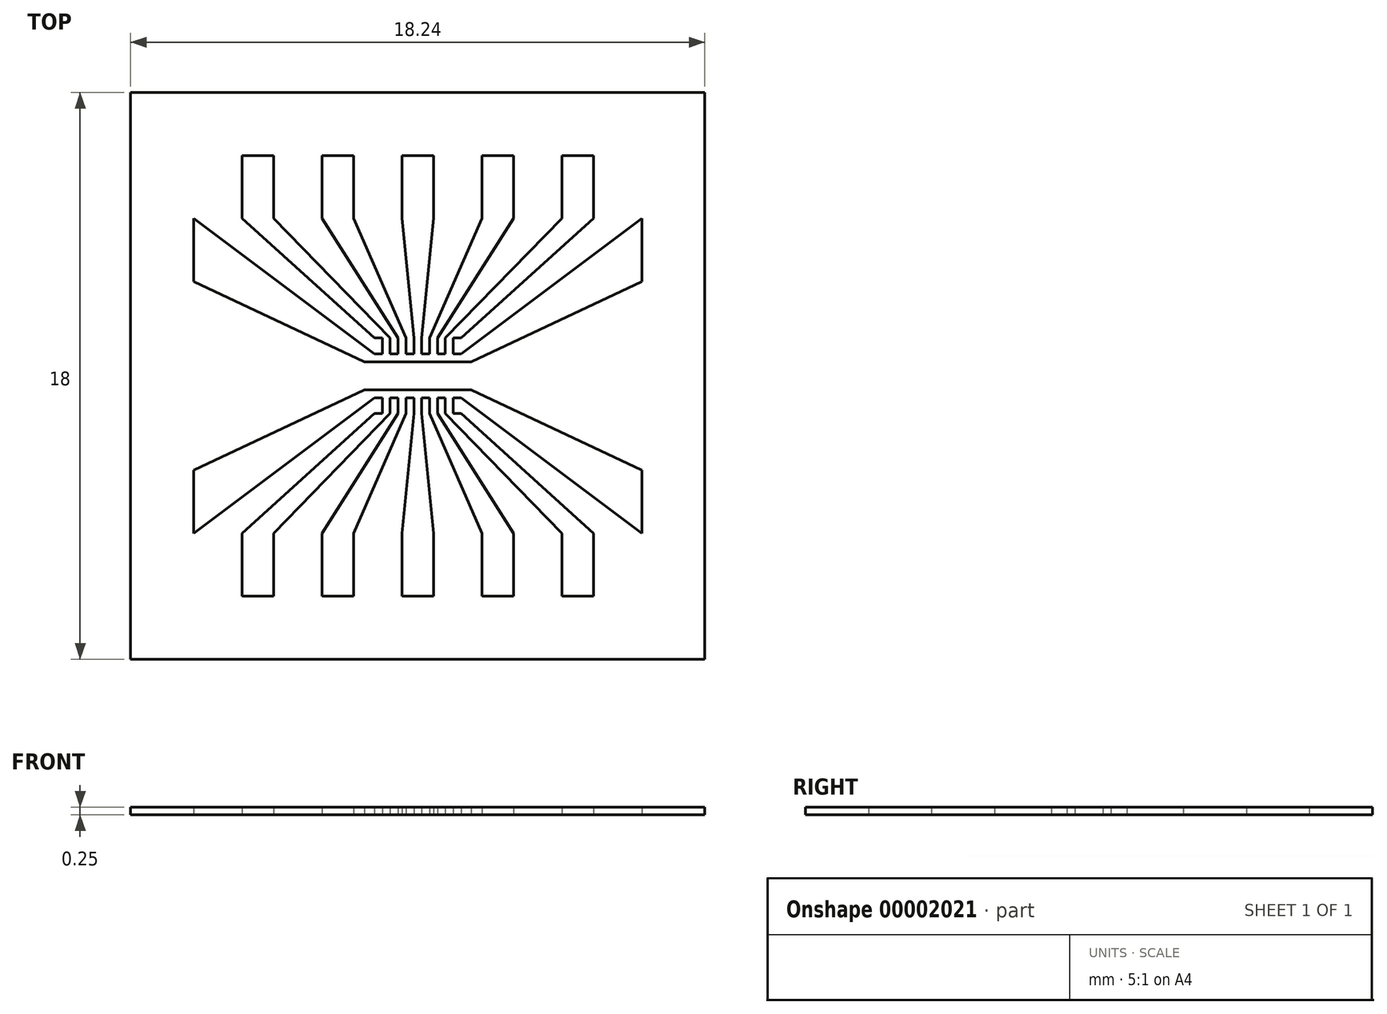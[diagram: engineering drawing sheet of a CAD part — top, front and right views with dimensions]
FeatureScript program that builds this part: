
annotation { "Feature Type Name" : "Feature", "Feature Type Description" : "" }
export const myFeature = defineFeature(function(context is Context, id is Id, definition is map)
    precondition{}
    {
        {
            var Q0;
            Q0=qCreatedBy(makeId("Top.planeOp"),FACE);
            var sketch = newSketch(context, id + "F0", { "sketchPlane" : qUnion([Q0])});
            skLineSegment(sketch, "E0.rect.bottom", {"start": v(1.7, 0.45) * mm, "end": v(-1.7, 0.45) * mm});
            skLineSegment(sketch, "E0.rect.top", {"start": v(1.7, -0.45) * mm, "end": v(-1.7, -0.45) * mm});
            skLineSegment(sketch, "E0.rect.left", {"start": v(1.7, 0.45) * mm, "end": v(1.7, -0.45) * mm, "construction": true});
            skLineSegment(sketch, "E0.rect.right", {"start": v(-1.7, 0.45) * mm, "end": v(-1.7, -0.45) * mm, "construction": true});
            skPoint(sketch, "E0.rect.middle", {"position": v(0, 0) * mm});
            skLineSegment(sketch, "E1", {"start": v(0, 0.45) * mm, "end": v(0, -0.45) * mm, "construction": true});
            skLineSegment(sketch, "E2", {"start": v(-1.7, 0) * mm, "end": v(1.7, 0) * mm, "construction": true});
            skLineSegment(sketch, "E3.bottom", {"start": v(-1.38, -0.7) * mm, "end": v(-1.13, -0.7) * mm});
            skLineSegment(sketch, "E3.top", {"start": v(-1.38, -1.2) * mm, "end": v(-1.13, -1.2) * mm});
            skLineSegment(sketch, "E3.left", {"start": v(-1.38, -0.7) * mm, "end": v(-1.38, -1.2) * mm, "construction": true});
            skLineSegment(sketch, "E3.right", {"start": v(-1.12, -0.7) * mm, "end": v(-1.12, -1.2) * mm});
            skLineSegment(sketch, "E4.bottom", {"start": v(-0.88, -0.7) * mm, "end": v(-0.63, -0.7) * mm});
            skLineSegment(sketch, "E4.top", {"start": v(-0.88, -1.2) * mm, "end": v(-0.63, -1.2) * mm, "construction": true});
            skLineSegment(sketch, "E4.left", {"start": v(-0.88, -0.7) * mm, "end": v(-0.88, -1.2) * mm});
            skLineSegment(sketch, "E4.right", {"start": v(-0.63, -0.7) * mm, "end": v(-0.63, -1.2) * mm});
            skLineSegment(sketch, "E5.bottom", {"start": v(-0.38, -0.7) * mm, "end": v(-0.12, -0.7) * mm});
            skLineSegment(sketch, "E5.top", {"start": v(-0.38, -1.2) * mm, "end": v(-0.13, -1.2) * mm, "construction": true});
            skLineSegment(sketch, "E5.left", {"start": v(-0.38, -0.7) * mm, "end": v(-0.38, -1.2) * mm});
            skLineSegment(sketch, "E5.right", {"start": v(-0.12, -0.7) * mm, "end": v(-0.12, -1.2) * mm});
            skLineSegment(sketch, "E6.bottom", {"start": v(0.12, -0.7) * mm, "end": v(0.38, -0.7) * mm});
            skLineSegment(sketch, "E6.top", {"start": v(0.13, -1.2) * mm, "end": v(0.38, -1.2) * mm, "construction": true});
            skLineSegment(sketch, "E6.left", {"start": v(0.12, -0.7) * mm, "end": v(0.12, -1.2) * mm});
            skLineSegment(sketch, "E6.right", {"start": v(0.38, -0.7) * mm, "end": v(0.38, -1.2) * mm});
            skLineSegment(sketch, "E7.bottom", {"start": v(0.63, -0.7) * mm, "end": v(0.88, -0.7) * mm});
            skLineSegment(sketch, "E7.top", {"start": v(0.63, -1.2) * mm, "end": v(0.88, -1.2) * mm, "construction": true});
            skLineSegment(sketch, "E7.left", {"start": v(0.63, -0.7) * mm, "end": v(0.63, -1.2) * mm});
            skLineSegment(sketch, "E7.right", {"start": v(0.88, -0.7) * mm, "end": v(0.88, -1.2) * mm});
            skLineSegment(sketch, "E8.bottom", {"start": v(1.13, -0.7) * mm, "end": v(1.38, -0.7) * mm});
            skLineSegment(sketch, "E8.top", {"start": v(1.13, -1.2) * mm, "end": v(1.38, -1.2) * mm});
            skLineSegment(sketch, "E8.left", {"start": v(1.12, -0.7) * mm, "end": v(1.12, -1.2) * mm});
            skLineSegment(sketch, "E8.right", {"start": v(1.38, -0.7) * mm, "end": v(1.38, -1.2) * mm, "construction": true});
            skLineSegment(sketch, "E9", {"start": v(-0.12, -0.7) * mm, "end": v(0.12, -0.7) * mm, "construction": true});
            skLineSegment(sketch, "E10", {"start": v(-0.63, -0.7) * mm, "end": v(-0.38, -0.7) * mm, "construction": true});
            skLineSegment(sketch, "E11", {"start": v(-1.13, -0.7) * mm, "end": v(-0.88, -0.7) * mm, "construction": true});
            skLineSegment(sketch, "E12", {"start": v(0.38, -0.7) * mm, "end": v(0.63, -0.7) * mm, "construction": true});
            skLineSegment(sketch, "E13", {"start": v(0.88, -0.7) * mm, "end": v(1.13, -0.7) * mm, "construction": true});
            skPoint(sketch, "E14", {"position": v(0, -0.7) * mm});
            skPoint(sketch, "E15", {"position": v(-1.25, -0.7) * mm});
            skPoint(sketch, "E16", {"position": v(-0.75, -0.7) * mm});
            skLineSegment(sketch, "E17.0.MirrorCS", {"start": v(0.12, 0.7) * mm, "end": v(0.12, 1.2) * mm});
            skLineSegment(sketch, "E17.1.MirrorCS", {"start": v(1.12, 0.7) * mm, "end": v(1.12, 1.2) * mm});
            skLineSegment(sketch, "E17.2.MirrorCS", {"start": v(0.63, 1.2) * mm, "end": v(0.88, 1.2) * mm, "construction": true});
            skLineSegment(sketch, "E17.3.MirrorCS", {"start": v(0.13, 0.7) * mm, "end": v(0.38, 0.7) * mm});
            skLineSegment(sketch, "E17.4.MirrorCS", {"start": v(0.88, 0.7) * mm, "end": v(1.13, 0.7) * mm, "construction": true});
            skLineSegment(sketch, "E17.5.MirrorCS", {"start": v(0.63, 0.7) * mm, "end": v(0.88, 0.7) * mm});
            skLineSegment(sketch, "E17.6.MirrorCS", {"start": v(-0.13, 0.7) * mm, "end": v(0.13, 0.7) * mm, "construction": true});
            skLineSegment(sketch, "E17.7.MirrorCS", {"start": v(-0.63, 0.7) * mm, "end": v(-0.38, 0.7) * mm, "construction": true});
            skLineSegment(sketch, "E17.8.MirrorCS", {"start": v(-0.63, 0.7) * mm, "end": v(-0.63, 1.2) * mm});
            skLineSegment(sketch, "E17.9.MirrorCS", {"start": v(0.88, 0.7) * mm, "end": v(0.88, 1.2) * mm});
            skLineSegment(sketch, "E17.10.MirrorCS", {"start": v(-0.38, 1.2) * mm, "end": v(-0.13, 1.2) * mm, "construction": true});
            skLineSegment(sketch, "E17.11.MirrorCS", {"start": v(1.13, 1.2) * mm, "end": v(1.38, 1.2) * mm});
            skLineSegment(sketch, "E17.12.MirrorCS", {"start": v(0.13, 1.2) * mm, "end": v(0.38, 1.2) * mm, "construction": true});
            skLineSegment(sketch, "E17.13.MirrorCS", {"start": v(-0.38, 0.7) * mm, "end": v(-0.38, 1.2) * mm});
            skLineSegment(sketch, "E17.14.MirrorCS", {"start": v(-0.38, 0.7) * mm, "end": v(-0.13, 0.7) * mm});
            skLineSegment(sketch, "E17.15.MirrorCS", {"start": v(1.13, 0.7) * mm, "end": v(1.38, 0.7) * mm});
            skLineSegment(sketch, "E17.16.MirrorCS", {"start": v(0.38, 0.7) * mm, "end": v(0.63, 0.7) * mm, "construction": true});
            skLineSegment(sketch, "E17.17.MirrorCS", {"start": v(-1.13, 0.7) * mm, "end": v(-0.88, 0.7) * mm, "construction": true});
            skLineSegment(sketch, "E17.18.MirrorCS", {"start": v(-1.38, 0.7) * mm, "end": v(-1.38, 1.2) * mm, "construction": true});
            skLineSegment(sketch, "E17.19.MirrorCS", {"start": v(-1.38, 1.2) * mm, "end": v(-1.13, 1.2) * mm});
            skLineSegment(sketch, "E17.20.MirrorCS", {"start": v(-0.88, 0.7) * mm, "end": v(-0.63, 0.7) * mm});
            skLineSegment(sketch, "E17.21.MirrorCS", {"start": v(-1.12, 0.7) * mm, "end": v(-1.12, 1.2) * mm});
            skLineSegment(sketch, "E17.22.MirrorCS", {"start": v(-1.38, 0.7) * mm, "end": v(-1.13, 0.7) * mm});
            skLineSegment(sketch, "E17.23.MirrorCS", {"start": v(-0.88, 0.7) * mm, "end": v(-0.88, 1.2) * mm});
            skLineSegment(sketch, "E17.24.MirrorCS", {"start": v(0.62, 0.7) * mm, "end": v(0.62, 1.2) * mm});
            skLineSegment(sketch, "E17.25.MirrorCS", {"start": v(1.38, 0.7) * mm, "end": v(1.38, 1.2) * mm, "construction": true});
            skLineSegment(sketch, "E17.26.MirrorCS", {"start": v(0.38, 0.7) * mm, "end": v(0.38, 1.2) * mm});
            skLineSegment(sketch, "E17.27.MirrorCS", {"start": v(-0.12, 0.7) * mm, "end": v(-0.13, 1.2) * mm});
            skLineSegment(sketch, "E17.28.MirrorCS", {"start": v(-0.88, 1.2) * mm, "end": v(-0.63, 1.2) * mm, "construction": true});
            skLineSegment(sketch, "E18.rect.bottom", {"start": v(-0.5, -5) * mm, "end": v(-2.04, -5) * mm, "construction": true});
            skLineSegment(sketch, "E18.rect.top", {"start": v(-0.5, -7) * mm, "end": v(-2.04, -7) * mm});
            skLineSegment(sketch, "E18.rect.left", {"start": v(-0.5, -5) * mm, "end": v(-0.5, -7) * mm});
            skLineSegment(sketch, "E18.rect.right", {"start": v(-2.04, -5) * mm, "end": v(-2.04, -7) * mm});
            skPoint(sketch, "E18.rect.middle", {"position": v(-1.27, -6) * mm});
            skLineSegment(sketch, "E19.rect.bottom", {"start": v(2.04, -5) * mm, "end": v(0.5, -5) * mm, "construction": true});
            skLineSegment(sketch, "E19.rect.top", {"start": v(2.04, -7) * mm, "end": v(0.5, -7) * mm});
            skLineSegment(sketch, "E19.rect.left", {"start": v(2.04, -5) * mm, "end": v(2.04, -7) * mm});
            skLineSegment(sketch, "E19.rect.right", {"start": v(0.5, -5) * mm, "end": v(0.5, -7) * mm});
            skPoint(sketch, "E19.rect.middle", {"position": v(1.27, -6) * mm});
            skLineSegment(sketch, "E20.rect.bottom", {"start": v(4.58, -5) * mm, "end": v(3.04, -5) * mm, "construction": true});
            skLineSegment(sketch, "E20.rect.top", {"start": v(4.58, -7) * mm, "end": v(3.04, -7) * mm});
            skLineSegment(sketch, "E20.rect.left", {"start": v(4.58, -5) * mm, "end": v(4.58, -7) * mm});
            skLineSegment(sketch, "E20.rect.right", {"start": v(3.04, -5) * mm, "end": v(3.04, -7) * mm});
            skPoint(sketch, "E20.rect.middle", {"position": v(3.8, -6) * mm});
            skLineSegment(sketch, "E21.rect.bottom", {"start": v(7.12, -5) * mm, "end": v(5.58, -5) * mm, "construction": true});
            skLineSegment(sketch, "E21.rect.top", {"start": v(7.12, -7) * mm, "end": v(5.58, -7) * mm});
            skLineSegment(sketch, "E21.rect.left", {"start": v(7.12, -5) * mm, "end": v(7.12, -7) * mm});
            skLineSegment(sketch, "E21.rect.right", {"start": v(5.58, -5) * mm, "end": v(5.58, -7) * mm});
            skPoint(sketch, "E21.rect.middle", {"position": v(6.35, -6) * mm});
            skLineSegment(sketch, "E22.rect.bottom", {"start": v(-3.04, -5) * mm, "end": v(-4.58, -5) * mm, "construction": true});
            skLineSegment(sketch, "E22.rect.top", {"start": v(-3.04, -7) * mm, "end": v(-4.58, -7) * mm});
            skLineSegment(sketch, "E22.rect.left", {"start": v(-3.04, -5) * mm, "end": v(-3.04, -7) * mm});
            skLineSegment(sketch, "E22.rect.right", {"start": v(-4.58, -5) * mm, "end": v(-4.58, -7) * mm});
            skPoint(sketch, "E22.rect.middle", {"position": v(-3.8, -6) * mm});
            skLineSegment(sketch, "E23.rect.bottom", {"start": v(-5.58, -5) * mm, "end": v(-7.12, -5) * mm, "construction": true});
            skLineSegment(sketch, "E23.rect.top", {"start": v(-5.58, -7) * mm, "end": v(-7.12, -7) * mm});
            skLineSegment(sketch, "E23.rect.left", {"start": v(-5.58, -5) * mm, "end": v(-5.58, -7) * mm});
            skLineSegment(sketch, "E23.rect.right", {"start": v(-7.12, -5) * mm, "end": v(-7.12, -7) * mm});
            skPoint(sketch, "E23.rect.middle", {"position": v(-6.35, -6) * mm});
            skLineSegment(sketch, "E24", {"start": v(-0.5, -5) * mm, "end": v(0.5, -5) * mm, "construction": true});
            skLineSegment(sketch, "E25", {"start": v(2.04, -5) * mm, "end": v(3.04, -5) * mm, "construction": true});
            skLineSegment(sketch, "E26", {"start": v(4.58, -5) * mm, "end": v(5.58, -5) * mm, "construction": true});
            skLineSegment(sketch, "E27", {"start": v(-2.04, -5) * mm, "end": v(-3.04, -5) * mm, "construction": true});
            skLineSegment(sketch, "E28", {"start": v(-4.58, -5) * mm, "end": v(-5.58, -5) * mm, "construction": true});
            skPoint(sketch, "E29", {"position": v(0, -5) * mm});
            skLineSegment(sketch, "E30", {"start": v(-0.12, -1.2) * mm, "end": v(-0.5, -5) * mm});
            skLineSegment(sketch, "E31", {"start": v(-0.38, -1.2) * mm, "end": v(-2.04, -5) * mm});
            skLineSegment(sketch, "E32", {"start": v(-0.62, -1.2) * mm, "end": v(-3.04, -5) * mm});
            skLineSegment(sketch, "E33", {"start": v(-0.88, -1.2) * mm, "end": v(-4.58, -5) * mm});
            skLineSegment(sketch, "E34", {"start": v(0.13, -1.2) * mm, "end": v(0.5, -5) * mm});
            skLineSegment(sketch, "E35", {"start": v(0.38, -1.2) * mm, "end": v(2.04, -5) * mm});
            skLineSegment(sketch, "E36", {"start": v(0.62, -1.2) * mm, "end": v(3.04, -5) * mm});
            skLineSegment(sketch, "E37", {"start": v(0.88, -1.2) * mm, "end": v(4.58, -5) * mm});
            skLineSegment(sketch, "E38", {"start": v(-1.38, -1.2) * mm, "end": v(-5.58, -5) * mm});
            skLineSegment(sketch, "E39", {"start": v(-1.38, -0.7) * mm, "end": v(-7.12, -5) * mm});
            skLineSegment(sketch, "E40", {"start": v(1.38, -1.2) * mm, "end": v(5.58, -5) * mm});
            skLineSegment(sketch, "E41", {"start": v(1.37, -0.7) * mm, "end": v(7.12, -5) * mm});
            skLineSegment(sketch, "E42", {"start": v(7.12, 3) * mm, "end": v(7.12, -3) * mm});
            skLineSegment(sketch, "E43", {"start": v(7.12, 3) * mm, "end": v(1.7, 0.45) * mm});
            skLineSegment(sketch, "E44", {"start": v(7.12, -3) * mm, "end": v(1.7, -0.45) * mm});
            skPoint(sketch, "E45", {"position": v(7.12, 0) * mm});
            skLineSegment(sketch, "E46", {"start": v(-7.12, 3) * mm, "end": v(-7.12, -3) * mm});
            skLineSegment(sketch, "E47", {"start": v(-7.12, 3) * mm, "end": v(-1.7, 0.45) * mm});
            skLineSegment(sketch, "E48", {"start": v(-7.12, -3) * mm, "end": v(-1.7, -0.45) * mm});
            skLineSegment(sketch, "E49.0.MirrorCS", {"start": v(-0.5, 5) * mm, "end": v(-0.5, 7) * mm});
            skPoint(sketch, "E49.1.MirrorP", {"position": v(-1.27, 6) * mm});
            skLineSegment(sketch, "E49.2.MirrorCS", {"start": v(4.58, 7) * mm, "end": v(3.04, 7) * mm});
            skLineSegment(sketch, "E49.3.MirrorCS", {"start": v(2.04, 5) * mm, "end": v(3.04, 5) * mm, "construction": true});
            skLineSegment(sketch, "E49.4.MirrorCS", {"start": v(-3.04, 7) * mm, "end": v(-4.58, 7) * mm});
            skLineSegment(sketch, "E49.5.MirrorCS", {"start": v(-0.5, 7) * mm, "end": v(-2.04, 7) * mm});
            skLineSegment(sketch, "E49.6.MirrorCS", {"start": v(0.13, 1.2) * mm, "end": v(0.5, 5) * mm});
            skLineSegment(sketch, "E49.7.MirrorCS", {"start": v(1.38, 1.2) * mm, "end": v(5.58, 5) * mm});
            skLineSegment(sketch, "E49.8.MirrorCS", {"start": v(-7.12, 5) * mm, "end": v(-7.12, 7) * mm});
            skLineSegment(sketch, "E49.9.MirrorCS", {"start": v(0.5, 5) * mm, "end": v(0.5, 7) * mm});
            skPoint(sketch, "E49.10.MirrorP", {"position": v(-6.35, 6) * mm});
            skLineSegment(sketch, "E49.11.MirrorCS", {"start": v(7.12, 5) * mm, "end": v(5.58, 5) * mm, "construction": true});
            skLineSegment(sketch, "E49.12.MirrorCS", {"start": v(-4.58, 5) * mm, "end": v(-5.58, 5) * mm, "construction": true});
            skLineSegment(sketch, "E49.13.MirrorCS", {"start": v(-0.5, 5) * mm, "end": v(-2.04, 5) * mm, "construction": true});
            skLineSegment(sketch, "E49.14.MirrorCS", {"start": v(-0.88, 1.2) * mm, "end": v(-4.58, 5) * mm});
            skLineSegment(sketch, "E49.15.MirrorCS", {"start": v(-3.04, 5) * mm, "end": v(-4.58, 5) * mm, "construction": true});
            skLineSegment(sketch, "E49.16.MirrorCS", {"start": v(-0.62, 1.2) * mm, "end": v(-3.04, 5) * mm});
            skLineSegment(sketch, "E49.17.MirrorCS", {"start": v(5.58, 5) * mm, "end": v(5.58, 7) * mm});
            skLineSegment(sketch, "E49.18.MirrorCS", {"start": v(3.04, 5) * mm, "end": v(3.04, 7) * mm});
            skPoint(sketch, "E49.19.MirrorP", {"position": v(6.35, 6) * mm});
            skLineSegment(sketch, "E49.20.MirrorCS", {"start": v(-2.04, 5) * mm, "end": v(-3.04, 5) * mm, "construction": true});
            skLineSegment(sketch, "E49.21.MirrorCS", {"start": v(-1.38, 1.2) * mm, "end": v(-5.58, 5) * mm});
            skLineSegment(sketch, "E49.22.MirrorCS", {"start": v(2.04, 7) * mm, "end": v(0.5, 7) * mm});
            skLineSegment(sketch, "E49.23.MirrorCS", {"start": v(-5.58, 7) * mm, "end": v(-7.12, 7) * mm});
            skLineSegment(sketch, "E49.24.MirrorCS", {"start": v(-3.04, 5) * mm, "end": v(-3.04, 7) * mm});
            skLineSegment(sketch, "E49.25.MirrorCS", {"start": v(-0.12, 1.2) * mm, "end": v(-0.5, 5) * mm});
            skPoint(sketch, "E49.26.MirrorP", {"position": v(-3.8, 6) * mm});
            skLineSegment(sketch, "E49.27.MirrorCS", {"start": v(-5.58, 5) * mm, "end": v(-5.58, 7) * mm});
            skLineSegment(sketch, "E49.28.MirrorCS", {"start": v(2.04, 5) * mm, "end": v(2.04, 7) * mm});
            skLineSegment(sketch, "E49.29.MirrorCS", {"start": v(-1.37, 0.7) * mm, "end": v(-7.12, 5) * mm});
            skPoint(sketch, "E49.30.MirrorP", {"position": v(1.27, 6) * mm});
            skLineSegment(sketch, "E49.31.MirrorCS", {"start": v(2.04, 5) * mm, "end": v(0.5, 5) * mm, "construction": true});
            skLineSegment(sketch, "E49.32.MirrorCS", {"start": v(0.37, 1.2) * mm, "end": v(2.04, 5) * mm});
            skLineSegment(sketch, "E49.33.MirrorCS", {"start": v(0.88, 1.2) * mm, "end": v(4.58, 5) * mm});
            skLineSegment(sketch, "E49.34.MirrorCS", {"start": v(-5.58, 5) * mm, "end": v(-7.12, 5) * mm, "construction": true});
            skLineSegment(sketch, "E49.35.MirrorCS", {"start": v(-0.38, 1.2) * mm, "end": v(-2.04, 5) * mm});
            skLineSegment(sketch, "E49.36.MirrorCS", {"start": v(7.12, 7) * mm, "end": v(5.58, 7) * mm});
            skLineSegment(sketch, "E49.37.MirrorCS", {"start": v(0.62, 1.2) * mm, "end": v(3.04, 5) * mm});
            skLineSegment(sketch, "E49.38.MirrorCS", {"start": v(1.37, 0.7) * mm, "end": v(7.12, 5) * mm});
            skLineSegment(sketch, "E49.39.MirrorCS", {"start": v(7.12, 5) * mm, "end": v(7.12, 7) * mm});
            skLineSegment(sketch, "E49.40.MirrorCS", {"start": v(4.58, 5) * mm, "end": v(3.04, 5) * mm, "construction": true});
            skLineSegment(sketch, "E49.41.MirrorCS", {"start": v(-0.5, 5) * mm, "end": v(0.5, 5) * mm, "construction": true});
            skLineSegment(sketch, "E49.42.MirrorCS", {"start": v(4.58, 5) * mm, "end": v(5.58, 5) * mm, "construction": true});
            skLineSegment(sketch, "E49.43.MirrorCS", {"start": v(-4.58, 5) * mm, "end": v(-4.58, 7) * mm});
            skPoint(sketch, "E49.44.MirrorP", {"position": v(0, 5) * mm});
            skLineSegment(sketch, "E49.45.MirrorCS", {"start": v(4.58, 5) * mm, "end": v(4.58, 7) * mm});
            skLineSegment(sketch, "E49.46.MirrorCS", {"start": v(-2.04, 5) * mm, "end": v(-2.04, 7) * mm});
            skPoint(sketch, "E49.47.MirrorP", {"position": v(3.8, 6) * mm});
            skLineSegment(sketch, "E50.bottom", {"start": v(-7.12, 7) * mm, "end": v(7.12, 7) * mm});
            skLineSegment(sketch, "E50.top", {"start": v(-7.12, -7) * mm, "end": v(7.12, -7) * mm});
            skLineSegment(sketch, "E50.left", {"start": v(-7.12, 7) * mm, "end": v(-7.12, -7) * mm});
            skLineSegment(sketch, "E50.right", {"start": v(7.12, 7) * mm, "end": v(7.12, -7) * mm});
            skLineSegment(sketch, "E51.rect.bottom", {"start": v(9.12, 9) * mm, "end": v(-9.12, 9) * mm});
            skLineSegment(sketch, "E51.rect.top", {"start": v(9.12, -9) * mm, "end": v(-9.12, -9) * mm});
            skLineSegment(sketch, "E51.rect.left", {"start": v(9.12, 9) * mm, "end": v(9.12, -9) * mm});
            skLineSegment(sketch, "E51.rect.right", {"start": v(-9.12, 9) * mm, "end": v(-9.12, -9) * mm});
            skSolve(sketch);
        }
        {
            var Q0;
            Q0=makeQuery(id+"F0.imprint","IMPRINT",FACE,{"disambiguationData":[TD([[makeQuery(id+"F0.imprint","IMPRINT",EDGE,{"derivedFrom":sQuery(id+"F0.wireOp",EDGE,"E3.bottom")}),-1.0]])]});
            var Q1;
            Q1=makeQuery(id+"F0.imprint","IMPRINT",FACE,{"disambiguationData":[TD([[makeQuery(id+"F0.imprint","IMPRINT",EDGE,{"derivedFrom":sQuery(id+"F0.wireOp",EDGE,"E4.bottom")}),-1.0]])]});
            var Q2;
            Q2=makeQuery(id+"F0.imprint","IMPRINT",FACE,{"disambiguationData":[TD([[makeQuery(id+"F0.imprint","IMPRINT",EDGE,{"derivedFrom":sQuery(id+"F0.wireOp",EDGE,"E51.rect.bottom")}),1.0]])]});
            var Q3;
            Q3=makeQuery(id+"F0.imprint","IMPRINT",FACE,{"disambiguationData":[TD([[makeQuery(id+"F0.imprint","IMPRINT",EDGE,{"derivedFrom":sQuery(id+"F0.wireOp",EDGE,"E5.bottom")}),-1.0]])]});
            var Q4;
            Q4=makeQuery(id+"F0.imprint","IMPRINT",FACE,{"disambiguationData":[TD([[makeQuery(id+"F0.imprint","IMPRINT",EDGE,{"derivedFrom":sQuery(id+"F0.wireOp",EDGE,"E6.bottom")}),-1.0]])]});
            var Q5;
            Q5=makeQuery(id+"F0.imprint","IMPRINT",FACE,{"disambiguationData":[TD([[makeQuery(id+"F0.imprint","IMPRINT",EDGE,{"derivedFrom":sQuery(id+"F0.wireOp",EDGE,"E7.bottom")}),-1.0]])]});
            var Q6;
            Q6=makeQuery(id+"F0.imprint","IMPRINT",FACE,{"disambiguationData":[TD([[makeQuery(id+"F0.imprint","IMPRINT",EDGE,{"derivedFrom":sQuery(id+"F0.wireOp",EDGE,"E8.bottom")}),-1.0]])]});
            var Q7;
            Q7=makeQuery(id+"F0.imprint","IMPRINT",FACE,{"disambiguationData":[TD([[makeQuery(id+"F0.imprint","IMPRINT",EDGE,{"derivedFrom":sQuery(id+"F0.wireOp",EDGE,"E0.rect.bottom")}),1.0]])]});
            var Q8;
            Q8=makeQuery(id+"F0.imprint","IMPRINT",FACE,{"disambiguationData":[TD([[makeQuery(id+"F0.imprint","IMPRINT",EDGE,{"derivedFrom":sQuery(id+"F0.wireOp",EDGE,"E17.1.MirrorCS")}),-1.0]])]});
            var Q9;
            Q9=makeQuery(id+"F0.imprint","IMPRINT",FACE,{"disambiguationData":[TD([[makeQuery(id+"F0.imprint","IMPRINT",EDGE,{"derivedFrom":sQuery(id+"F0.wireOp",EDGE,"E17.5.MirrorCS")}),1.0]])]});
            var Q10;
            Q10=makeQuery(id+"F0.imprint","IMPRINT",FACE,{"disambiguationData":[TD([[makeQuery(id+"F0.imprint","IMPRINT",EDGE,{"derivedFrom":sQuery(id+"F0.wireOp",EDGE,"E17.0.MirrorCS")}),-1.0]])]});
            var Q11;
            Q11=makeQuery(id+"F0.imprint","IMPRINT",FACE,{"disambiguationData":[TD([[makeQuery(id+"F0.imprint","IMPRINT",EDGE,{"derivedFrom":sQuery(id+"F0.wireOp",EDGE,"E17.13.MirrorCS")}),-1.0]])]});
            var Q12;
            Q12=makeQuery(id+"F0.imprint","IMPRINT",FACE,{"disambiguationData":[TD([[makeQuery(id+"F0.imprint","IMPRINT",EDGE,{"derivedFrom":sQuery(id+"F0.wireOp",EDGE,"E17.8.MirrorCS")}),1.0]])]});
            var Q13;
            Q13=makeQuery(id+"F0.imprint","IMPRINT",FACE,{"disambiguationData":[TD([[makeQuery(id+"F0.imprint","IMPRINT",EDGE,{"derivedFrom":sQuery(id+"F0.wireOp",EDGE,"E17.19.MirrorCS")}),-1.0]])]});
            extrude(context, id + "F1", {"entities" : qUnion([Q0, Q1, Q2, Q3, Q4, Q5, Q6, Q7, Q8, Q9, Q10, Q11, Q12, Q13]), "depth" : .25 * mm});
        }
    });
